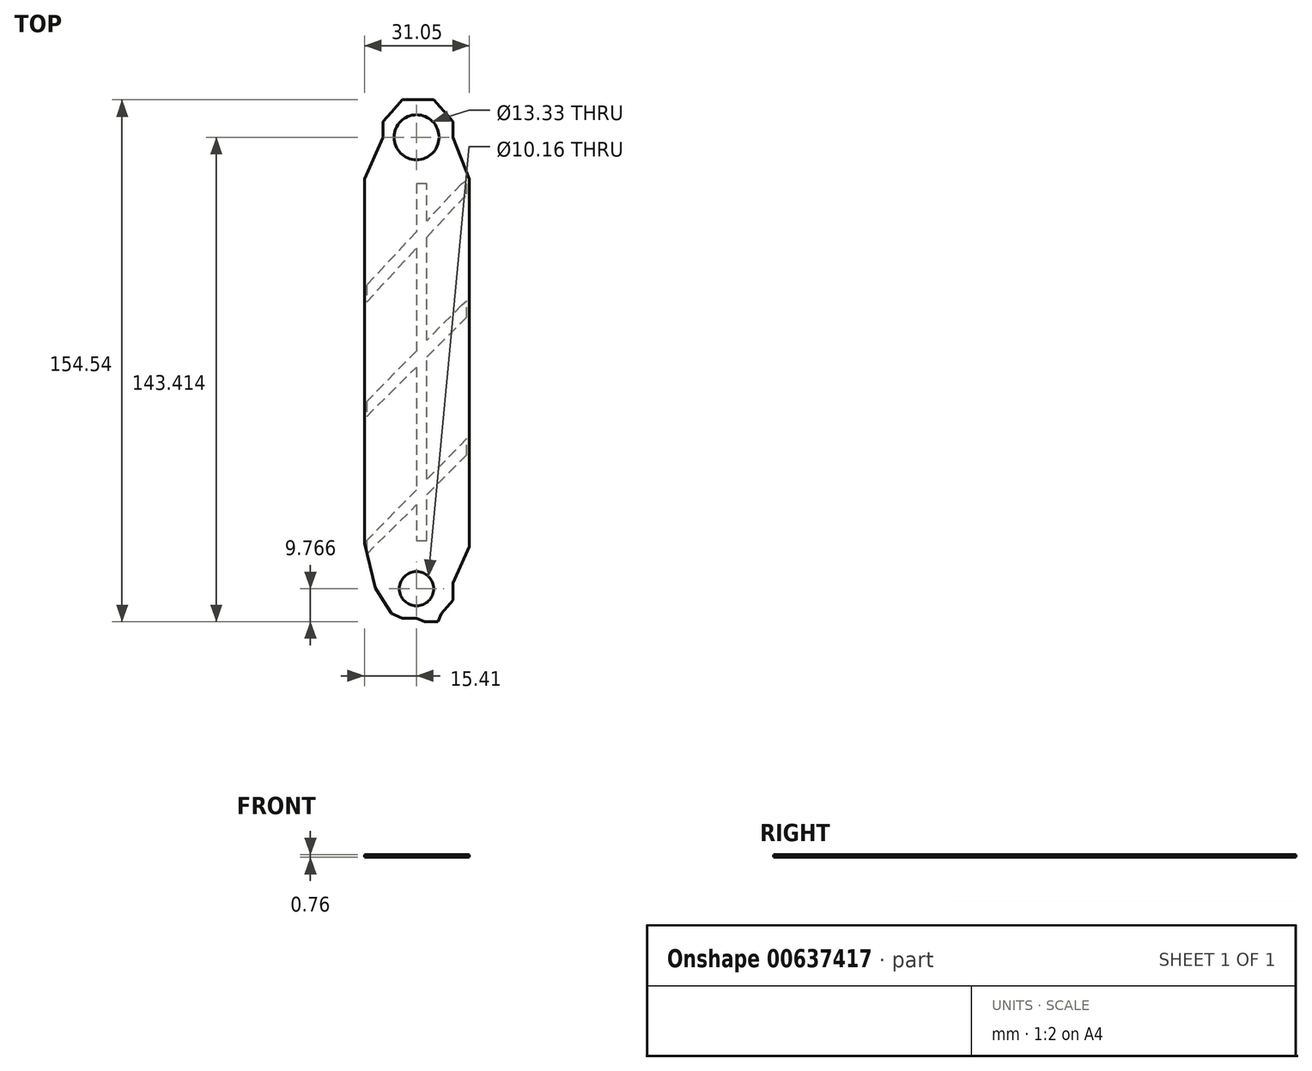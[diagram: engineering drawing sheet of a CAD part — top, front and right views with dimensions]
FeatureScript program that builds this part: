
annotation { "Feature Type Name" : "Feature", "Feature Type Description" : "" }
export const myFeature = defineFeature(function(context is Context, id is Id, definition is map)
    precondition{}
    {
        {
            var Q0;
            Q0=qCreatedBy(makeId("Top.planeOp"),FACE);
            var sketch = newSketch(context, id + "F0", { "sketchPlane" : qUnion([Q0])});
            skCircle(sketch, "E0", {"center": v(0, -64.92) * mm, "radius": 10.41 * mm});
            skCircle(sketch, "E1", {"center": v(0, 68.72) * mm, "radius": 10.32 * mm});
            skSolve(sketch);
        }
        {
            var Q0;
            Q0=qCreatedBy(makeId("Top.planeOp"),FACE);
            var sketch = newSketch(context, id + "F1", { "sketchPlane" : qUnion([Q0])});
            skLineSegment(sketch, "E2", {"start": v(0, 79.85) * mm, "end": v(-4.23, 79.85) * mm});
            skLineSegment(sketch, "E3", {"start": v(-4.23, 79.85) * mm, "end": v(-7.42, 76.2) * mm});
            skLineSegment(sketch, "E4", {"start": v(-7.42, 76.2) * mm, "end": v(-9.93, 73.46) * mm});
            skLineSegment(sketch, "E5", {"start": v(-9.93, 73.46) * mm, "end": v(-9.93, 68.66) * mm});
            skLineSegment(sketch, "E6", {"start": v(-9.93, 68.66) * mm, "end": v(-15.41, 56.33) * mm});
            skLineSegment(sketch, "E7", {"start": v(-15.41, 56.33) * mm, "end": v(-15.41, -51.43) * mm});
            skLineSegment(sketch, "E8", {"start": v(-15.41, -51.43) * mm, "end": v(-12.22, -64.67) * mm});
            skLineSegment(sketch, "E9", {"start": v(-12.22, -64.67) * mm, "end": v(-9.93, -68.32) * mm});
            skLineSegment(sketch, "E10", {"start": v(-9.93, -68.32) * mm, "end": v(-7.42, -72.2) * mm});
            skLineSegment(sketch, "E11", {"start": v(-7.42, -72.2) * mm, "end": v(-4.23, -73.63) * mm});
            skLineSegment(sketch, "E12", {"start": v(0, -73.63) * mm, "end": v(2.4, -74.7) * mm});
            skLineSegment(sketch, "E13", {"start": v(2.4, -74.7) * mm, "end": v(6.28, -74.7) * mm});
            skLineSegment(sketch, "E14", {"start": v(6.28, -74.7) * mm, "end": v(7.38, -72.2) * mm});
            skLineSegment(sketch, "E15", {"start": v(7.38, -72.2) * mm, "end": v(10.84, -68.32) * mm});
            skLineSegment(sketch, "E16", {"start": v(10.84, -68.32) * mm, "end": v(10.84, -63.3) * mm});
            skLineSegment(sketch, "E17", {"start": v(10.84, -63.3) * mm, "end": v(15.64, -52.5) * mm});
            skLineSegment(sketch, "E18", {"start": v(15.64, -7.14) * mm, "end": v(15.64, 14.55) * mm});
            skLineSegment(sketch, "E19", {"start": v(15.64, 14.55) * mm, "end": v(15.64, 38.07) * mm});
            skLineSegment(sketch, "E20", {"start": v(15.64, 38.07) * mm, "end": v(15.64, 52.45) * mm});
            skLineSegment(sketch, "E21", {"start": v(15.64, 52.45) * mm, "end": v(15.64, 56.33) * mm});
            skLineSegment(sketch, "E22", {"start": v(15.64, 56.33) * mm, "end": v(10.84, 68.66) * mm});
            skLineSegment(sketch, "E23", {"start": v(10.84, 68.66) * mm, "end": v(10.84, 73.46) * mm});
            skLineSegment(sketch, "E24", {"start": v(10.84, 73.46) * mm, "end": v(5.13, 79.85) * mm});
            skLineSegment(sketch, "E25", {"start": v(5.13, 79.85) * mm, "end": v(0, 79.85) * mm});
            skLineSegment(sketch, "E26", {"start": v(15.64, -7.14) * mm, "end": v(15.64, -52.5) * mm});
            skLineSegment(sketch, "E27", {"start": v(0, -73.63) * mm, "end": v(-4.23, -73.63) * mm});
            skSolve(sketch);
        }
        {
            var Q0;
            Q0=makeQuery(id+"F1.imprint","IMPRINT",FACE,{"disambiguationData":[TD([[makeQuery(id+"F1.imprint","IMPRINT",EDGE,{"derivedFrom":sQuery(id+"F1.wireOp",EDGE,"E2")}),1.0]])]});
            extrude(context, id + "F2", {"entities" : qUnion([Q0]), "depth" : 0.76 * mm, "offsetDistance" : 25.4 * mm});
        }
        {
            var Q0;
            Q0=sQuery(id+"F0.wireOp",VERTEX,"E1.center");
            var Q1;
            Q1=makeQuery(id+"F2.opExtrude","SWEPT_BODY",BODY,{"disambiguationData":[OSD([sQuery(id+"F1.wireOp",EDGE,"E2"),sQuery(id+"F1.wireOp",EDGE,"E3"),sQuery(id+"F1.wireOp",EDGE,"E4"),sQuery(id+"F1.wireOp",EDGE,"E5"),sQuery(id+"F1.wireOp",EDGE,"E6"),sQuery(id+"F1.wireOp",EDGE,"E7"),sQuery(id+"F1.wireOp",EDGE,"E8"),sQuery(id+"F1.wireOp",EDGE,"E9"),sQuery(id+"F1.wireOp",EDGE,"E10"),sQuery(id+"F1.wireOp",EDGE,"E11"),sQuery(id+"F1.wireOp",EDGE,"E12"),sQuery(id+"F1.wireOp",EDGE,"E13"),sQuery(id+"F1.wireOp",EDGE,"E14"),sQuery(id+"F1.wireOp",EDGE,"E15"),sQuery(id+"F1.wireOp",EDGE,"E16"),sQuery(id+"F1.wireOp",EDGE,"E17"),sQuery(id+"F1.wireOp",EDGE,"E18"),sQuery(id+"F1.wireOp",EDGE,"E19"),sQuery(id+"F1.wireOp",EDGE,"E20"),sQuery(id+"F1.wireOp",EDGE,"E21"),sQuery(id+"F1.wireOp",EDGE,"E22"),sQuery(id+"F1.wireOp",EDGE,"E23"),sQuery(id+"F1.wireOp",EDGE,"E24"),sQuery(id+"F1.wireOp",EDGE,"E25"),sQuery(id+"F1.wireOp",EDGE,"E26"),sQuery(id+"F1.wireOp",EDGE,"E27")])]});
            hole(context, id + "F3", {"style" : HoleStyle.SIMPLE, "endStyle" : HoleEndStyle.THROUGH, "oppositeDirection" : true, "holeDiameter" : 13.33 * mm, "majorDiameter" : 6.35 * mm, "isTappedThrough" : true, "tappedDepth" : 12.7 * mm, "tapClearance" : 3, "locations" : qUnion([Q0]), "scope" : qUnion([Q1])});
        }
        {
            var Q0;
            Q0=sQuery(id+"F0.wireOp",VERTEX,"E0.center");
            var Q1;
            Q1=makeQuery(id+"F2.opExtrude","SWEPT_BODY",BODY,{"disambiguationData":[OSD([sQuery(id+"F1.wireOp",EDGE,"E2"),sQuery(id+"F1.wireOp",EDGE,"E3"),sQuery(id+"F1.wireOp",EDGE,"E4"),sQuery(id+"F1.wireOp",EDGE,"E5"),sQuery(id+"F1.wireOp",EDGE,"E6"),sQuery(id+"F1.wireOp",EDGE,"E7"),sQuery(id+"F1.wireOp",EDGE,"E8"),sQuery(id+"F1.wireOp",EDGE,"E9"),sQuery(id+"F1.wireOp",EDGE,"E10"),sQuery(id+"F1.wireOp",EDGE,"E11"),sQuery(id+"F1.wireOp",EDGE,"E12"),sQuery(id+"F1.wireOp",EDGE,"E13"),sQuery(id+"F1.wireOp",EDGE,"E14"),sQuery(id+"F1.wireOp",EDGE,"E15"),sQuery(id+"F1.wireOp",EDGE,"E16"),sQuery(id+"F1.wireOp",EDGE,"E17"),sQuery(id+"F1.wireOp",EDGE,"E18"),sQuery(id+"F1.wireOp",EDGE,"E19"),sQuery(id+"F1.wireOp",EDGE,"E20"),sQuery(id+"F1.wireOp",EDGE,"E21"),sQuery(id+"F1.wireOp",EDGE,"E22"),sQuery(id+"F1.wireOp",EDGE,"E23"),sQuery(id+"F1.wireOp",EDGE,"E24"),sQuery(id+"F1.wireOp",EDGE,"E25"),sQuery(id+"F1.wireOp",EDGE,"E26"),sQuery(id+"F1.wireOp",EDGE,"E27")])]});
            hole(context, id + "F4", {"style" : HoleStyle.SIMPLE, "endStyle" : HoleEndStyle.THROUGH, "oppositeDirection" : true, "holeDiameter" : 10.16 * mm, "majorDiameter" : 6.35 * mm, "isTappedThrough" : true, "tappedDepth" : 12.7 * mm, "tapClearance" : 3, "locations" : qUnion([Q0]), "scope" : qUnion([Q1])});
        }
        {
            var Q0;
            Q0=qCreatedBy(makeId("Top.planeOp"),FACE);
            var sketch = newSketch(context, id + "F5", { "sketchPlane" : qUnion([Q0])});
            skLineSegment(sketch, "E28", {"start": v(13.33, 55.02) * mm, "end": v(-14.8, 24.95) * mm});
            skLineSegment(sketch, "E29", {"start": v(-14.8, 24.95) * mm, "end": v(-14.8, 19.93) * mm});
            skLineSegment(sketch, "E30", {"start": v(-14.8, 19.93) * mm, "end": v(14.9, 51.99) * mm});
            skLineSegment(sketch, "E31", {"start": v(14.9, 51.99) * mm, "end": v(14.9, 56) * mm});
            skLineSegment(sketch, "E32", {"start": v(13.33, 55.02) * mm, "end": v(14.9, 56) * mm});
            skLineSegment(sketch, "E33", {"start": v(13.33, 19.08) * mm, "end": v(-14.8, -9.57) * mm});
            skLineSegment(sketch, "E34", {"start": v(-14.8, -9.57) * mm, "end": v(-14.8, -13.98) * mm});
            skLineSegment(sketch, "E35", {"start": v(-14.8, -13.98) * mm, "end": v(14.9, 15.47) * mm});
            skLineSegment(sketch, "E36", {"start": v(14.9, 15.47) * mm, "end": v(14.9, 20.28) * mm});
            skLineSegment(sketch, "E37", {"start": v(13.33, 19.08) * mm, "end": v(14.9, 20.28) * mm});
            skLineSegment(sketch, "E38", {"start": v(14.9, -20.46) * mm, "end": v(-14.8, -50.7) * mm});
            skLineSegment(sketch, "E39", {"start": v(-14.8, -50.7) * mm, "end": v(-14.8, -54.74) * mm});
            skLineSegment(sketch, "E40", {"start": v(-14.8, -54.74) * mm, "end": v(14.9, -25.3) * mm});
            skLineSegment(sketch, "E41", {"start": v(14.9, -25.3) * mm, "end": v(14.9, -20.46) * mm});
            skLineSegment(sketch, "E42", {"start": v(0, 55.02) * mm, "end": v(0, -50.7) * mm});
            skLineSegment(sketch, "E43", {"start": v(0, -50.7) * mm, "end": v(3.02, -50.7) * mm});
            skLineSegment(sketch, "E44", {"start": v(3.02, -50.7) * mm, "end": v(3.02, 55.02) * mm});
            skLineSegment(sketch, "E45", {"start": v(3.02, 55.02) * mm, "end": v(0, 55.02) * mm});
            skSolve(sketch);
        }
        {
            var Q0;
            Q0 = qSketchRegion(id + "F5", true);
            extrude(context, id + "F6", {"entities" : qUnion([Q0]), "operationType" : NewBodyOperationType.REMOVE, "depth" : 0.23 * mm, "offsetDistance" : 25.4 * mm});
        }
    });
